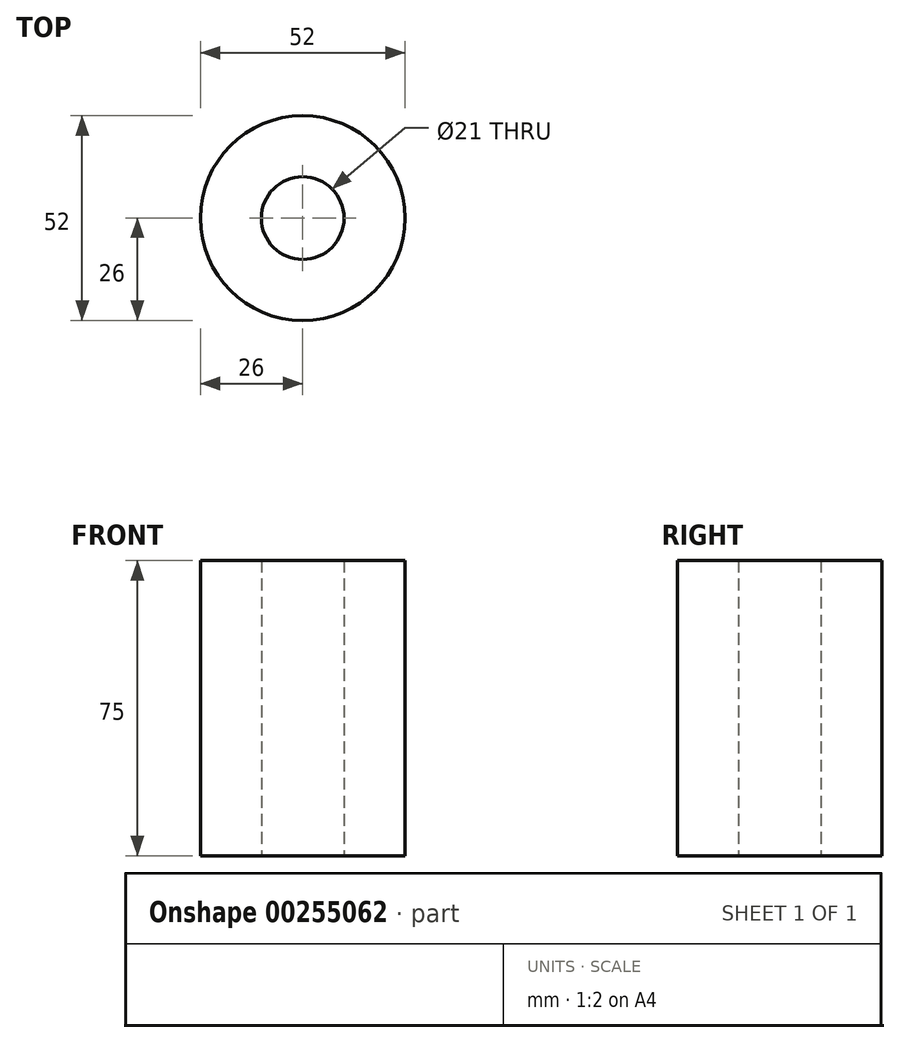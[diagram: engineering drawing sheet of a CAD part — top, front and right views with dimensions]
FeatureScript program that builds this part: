
annotation { "Feature Type Name" : "Feature", "Feature Type Description" : "" }
export const myFeature = defineFeature(function(context is Context, id is Id, definition is map)
    precondition{}
    {
        {
            var Q0;
            Q0=qCreatedBy(makeId("Top.planeOp"),FACE);
            var sketch = newSketch(context, id + "F0", { "sketchPlane" : qUnion([Q0])});
            skCircle(sketch, "E0", {"center": v(0, 0) * mm, "radius": 10.5 * mm});
            skCircle(sketch, "E1", {"center": v(0, 0) * mm, "radius": 26 * mm});
            skSolve(sketch);
        }
        {
            var Q0;
            Q0=makeQuery(id+"F0.imprint","IMPRINT",FACE,{"disambiguationData":[TD([[makeQuery(id+"F0.imprint","IMPRINT",EDGE,{"derivedFrom":sQuery(id+"F0.wireOp",EDGE,"E0")}),-1.0]])]});
            extrude(context, id + "F1", {"entities" : qUnion([Q0]), "offsetDistance" : 25 * mm, "depth" : 75 * mm});
        }
    });
